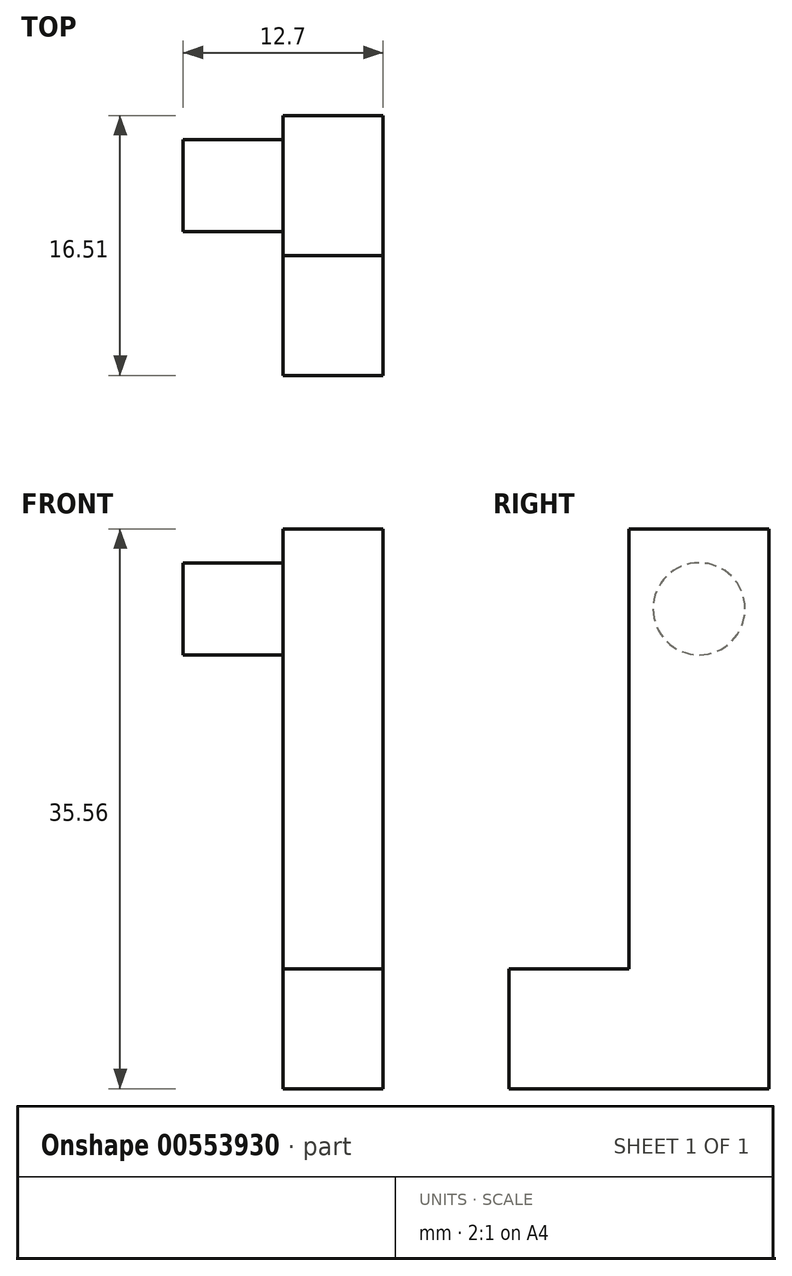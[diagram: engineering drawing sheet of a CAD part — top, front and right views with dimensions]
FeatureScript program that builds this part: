
annotation { "Feature Type Name" : "Feature", "Feature Type Description" : "" }
export const myFeature = defineFeature(function(context is Context, id is Id, definition is map)
    precondition{}
    {
        {
            var Q0;
            Q0=qCreatedBy(makeId("Right.planeOp"),FACE);
            var sketch = newSketch(context, id + "F0", { "sketchPlane" : qUnion([Q0])});
            skLineSegment(sketch, "E0", {"start": v(0, 0) * mm, "end": v(0, 35.56) * mm});
            skLineSegment(sketch, "E1", {"start": v(0, 35.56) * mm, "end": v(-8.9, 35.56) * mm});
            skLineSegment(sketch, "E2", {"start": v(-8.9, 35.56) * mm, "end": v(-8.9, 7.62) * mm});
            skLineSegment(sketch, "E3", {"start": v(-8.89, 7.62) * mm, "end": v(-16.51, 7.62) * mm});
            skLineSegment(sketch, "E4", {"start": v(-16.51, 7.62) * mm, "end": v(-16.51, 0) * mm});
            skLineSegment(sketch, "E5", {"start": v(-16.51, 0) * mm, "end": v(0, 0) * mm});
            skSolve(sketch);
        }
        {
            var Q0;
            Q0=makeQuery(id+"F0.imprint","IMPRINT",FACE,{"disambiguationData":[TD([[makeQuery(id+"F0.imprint","IMPRINT",EDGE,{"derivedFrom":sQuery(id+"F0.wireOp",EDGE,"E0")}),1.0]])]});
            extrude(context, id + "F1", {"entities" : qUnion([Q0]), "depth" : 6.35 * mm, "offsetDistance" : 25.4 * mm});
        }
        {
            var Q0;
            Q0=makeQuery(id+"F1.opExtrude","CAP_FACE",FACE,{"disambiguationData":[OSD([sQuery(id+"F0.wireOp",EDGE,"E0"),sQuery(id+"F0.wireOp",EDGE,"E1"),sQuery(id+"F0.wireOp",EDGE,"E2"),sQuery(id+"F0.wireOp",EDGE,"E3"),sQuery(id+"F0.wireOp",EDGE,"E4"),sQuery(id+"F0.wireOp",EDGE,"E5")])],"isStart":true});
            var sketch = newSketch(context, id + "F2", { "sketchPlane" : qUnion([Q0])});
            skCircle(sketch, "E6", {"center": v(4.45, 30.48) * mm, "radius": 2.92 * mm});
            skSolve(sketch);
        }
        {
            var Q0;
            Q0=makeQuery(id+"F2.imprint","IMPRINT",FACE,{"disambiguationData":[TD([[makeQuery(id+"F2.imprint","IMPRINT",EDGE,{"derivedFrom":sQuery(id+"F2.wireOp",EDGE,"E6")}),1.0]])]});
            extrude(context, id + "F3", {"entities" : qUnion([Q0]), "operationType" : NewBodyOperationType.ADD, "depth" : 6.35 * mm, "offsetDistance" : 25.4 * mm});
        }
    });
